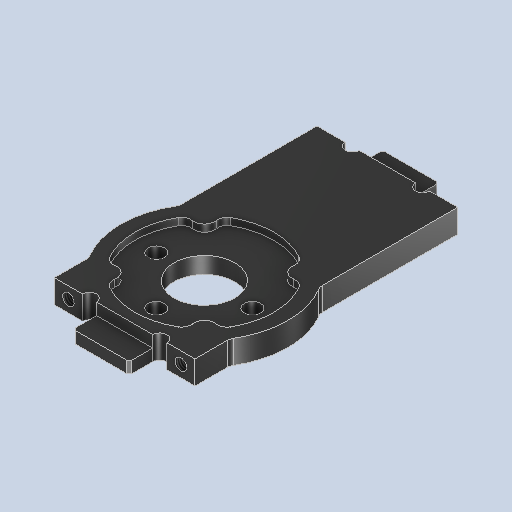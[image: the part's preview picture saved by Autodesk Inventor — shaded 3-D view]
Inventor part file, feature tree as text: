
AUTODESK INVENTOR PART (.ipt)
format: ipt  version: 2024.2 (Build 282272000, 272)  size: 347,648 bytes
history: native  units: mm
features: other x4, sketch x4, extrude x3, hole x3, fillet x2, mirror x2, plane x1, chamfer x1
ambient origin geometry x8: Origin, YZ Plane, XZ Plane, XY Plane, X Axis, Y Axis, Z Axis, Center Point
bodies: Solid2 (feature_tree)
feature tree (20):
  other  "CrossRollerBearingInnerSupportStand.ipt"
  sketch  "Sketch3"  dims[d5=5.0mm d7=0.05mm]
  extrude  "Extrusion1"  Depth=56.0mm
  extrude  "Extrusion2"  Depth=1.5mm
  fillet  "Fillet1"  Radius=12.0mm
  hole  "Hole1"  [1 undecoded]
  hole  "Hole2"  [1 undecoded]
  fillet  "Fillet2"  Radius=40.0mm
  hole  "Hole3"  [1 undecoded]
  mirror  "Mirror1"
  plane  "Work Plane1"
  mirror  "Mirror2"
  extrude  "Extrusion3"  Depth=3.0mm
  chamfer  "Chamfer1"  Distance=5.0mm
  other  "TaggingFeature1"
  sketch  "Sketch1"  dims[d0=10.0mm d1=56.0mm]
  sketch  "Sketch2"  dims[d2=30.0mm d3=1.5mm d4=12.0mm]
  sketch  "Sketch4"  dims[d8=0.05mm d9=2.0mm d10=40.0mm d12=360.0deg d14=17.0mm d15=3.0mm d16=5.0mm d17=0.0mm d18=1.5mm d19=0.0mm d20=2.0mm d21=13.0mm d22=3.5mm d23=5.2mm d24=5.1mm d25=4.5mm d26=90.0deg d27=8.0mm d28=20.594885mm d29=13.0mm d30=6.0mm d31=4.0mm d32=2.0mm d33=90.0deg d34=8.0mm d35=20.594885mm d36=2.0mm d38=4.0mm d39=2.459mm d40=6.0mm d41=4.0mm d42=2.0mm d43=90.0deg d44=4.0mm d45=0.0mm d46=2.5mm d47=0.0mm d48=0.5mm d49=2.0mm d50=45.0deg d51=24.0mm]
  other  "Solid2::CrossRollerBearingInnerSupportStand.ipt"
  other  "Srf1"
note: 3 required parameter values undecoded (feature->parameter linkage not recoverable at this tier; creation-order binding heuristic only, values carry confidence <= 0.55)
